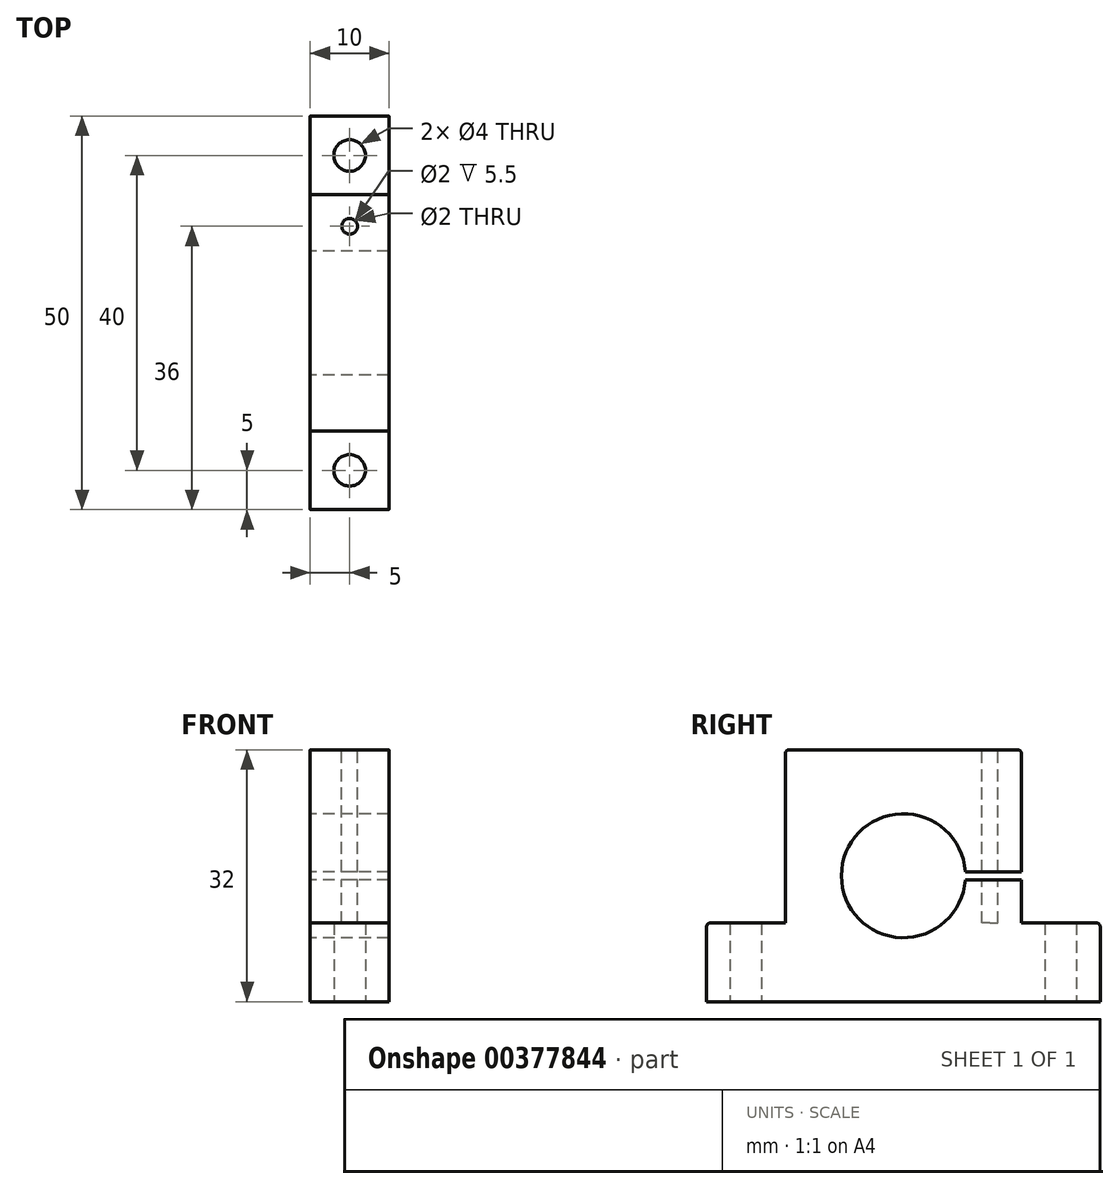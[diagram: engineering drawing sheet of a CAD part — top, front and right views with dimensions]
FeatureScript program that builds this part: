
annotation { "Feature Type Name" : "Feature", "Feature Type Description" : "" }
export const myFeature = defineFeature(function(context is Context, id is Id, definition is map)
    precondition{}
    {
        {
            var Q0;
            Q0=qCreatedBy(makeId("Right.planeOp"),FACE);
            var sketch = newSketch(context, id + "F0", { "sketchPlane" : qUnion([Q0])});
            skLineSegment(sketch, "E0.bottom", {"start": v(15, 16) * mm, "end": v(-15, 16) * mm});
            skLineSegment(sketch, "E0.top", {"start": v(15, -16) * mm, "end": v(-15, -16) * mm});
            skLineSegment(sketch, "E0.left", {"start": v(15, 16) * mm, "end": v(15, 0.5) * mm});
            skLineSegment(sketch, "E0.right", {"start": v(-15, 16) * mm, "end": v(-15, -16) * mm});
            skPoint(sketch, "E0.middle", {"position": v(0, 0) * mm});
            skArc(sketch, "E1", {"start": v(7.86, 0.5) * mm, "mid": v(-7.88, 0) * mm, "end": v(7.86, -0.5) * mm});
            skLineSegment(sketch, "E2", {"start": v(7.86, 0.5) * mm, "end": v(15, 0.5) * mm});
            skLineSegment(sketch, "E3", {"start": v(7.86, -0.5) * mm, "end": v(15, -0.5) * mm});
            skLineSegment(sketch, "E4", {"start": v(0, 0) * mm, "end": v(26.33, 0) * mm, "construction": true});
            skLineSegment(sketch, "E5.trimOffspring", {"start": v(15, -0.5) * mm, "end": v(15, -16) * mm});
            skSolve(sketch);
        }
        {
            var Q0;
            Q0 = qSketchRegion(id + "F0", true);
            extrude(context, id + "F1", {"entities" : qUnion([Q0]), "depth" : 5 * mm, "hasSecondDirection" : true, "secondDirectionOppositeDirection" : true, "secondDirectionDepth" : 5 * mm});
        }
        {
            var Q0;
            Q0=makeQuery(id+"F1.opExtrude","SWEPT_FACE",FACE,{"disambiguationData":[OSD([sQuery(id+"F0.wireOp",EDGE,"E0.bottom")])]});
            var sketch = newSketch(context, id + "F2", { "sketchPlane" : qUnion([Q0])});
            skCircle(sketch, "E6", {"center": v(0, 11) * mm, "radius": 1 * mm});
            skSolve(sketch);
        }
        {
            var Q0;
            Q0 = qSketchRegion(id + "F2", true);
            extrude(context, id + "F3", {"entities" : qUnion([Q0]), "operationType" : NewBodyOperationType.REMOVE, "endBound" : BoundingType.THROUGH_ALL, "oppositeDirection" : true, "depth" : 25 * mm});
        }
        {
            var Q0;
            Q0=makeQuery(id+"F1.opExtrude","SWEPT_FACE",FACE,{"disambiguationData":[OSD([sQuery(id+"F0.wireOp",EDGE,"E0.top")])]});
            var sketch = newSketch(context, id + "F4", { "sketchPlane" : qUnion([Q0])});
            skLineSegment(sketch, "E7.bottom", {"start": v(5, -25) * mm, "end": v(-5, -25) * mm});
            skLineSegment(sketch, "E7.top", {"start": v(5, 25) * mm, "end": v(-5, 25) * mm});
            skLineSegment(sketch, "E7.left", {"start": v(5, -25) * mm, "end": v(5, 25) * mm});
            skLineSegment(sketch, "E7.right", {"start": v(-5, -25) * mm, "end": v(-5, 25) * mm});
            skPoint(sketch, "E7.middle", {"position": v(0, 0) * mm});
            skCircle(sketch, "E8", {"center": v(0, 20) * mm, "radius": 2 * mm});
            skPoint(sketch, "E8.centerSnap0", {"position": v(0, 15) * mm});
            skCircle(sketch, "E9", {"center": v(0, -20) * mm, "radius": 2 * mm});
            skSolve(sketch);
        }
        {
            var Q0;
            Q0 = qSketchRegion(id + "F4", true);
            extrude(context, id + "F5", {"entities" : qUnion([Q0]), "operationType" : NewBodyOperationType.ADD, "oppositeDirection" : true, "depth" : 10 * mm});
        }
        {
            var Q0;
            Q0=makeQuery(id+"F5.boolean.opBoolean","MERGE",FACE,{"derivedFrom":[makeQuery(id+"F1.opExtrude","CAP_FACE",FACE,{"disambiguationData":[OSD([sQuery(id+"F0.wireOp",EDGE,"E0.bottom"),sQuery(id+"F0.wireOp",EDGE,"E0.top"),sQuery(id+"F0.wireOp",EDGE,"E0.left"),sQuery(id+"F0.wireOp",EDGE,"E0.right"),sQuery(id+"F0.wireOp",EDGE,"E1"),sQuery(id+"F0.wireOp",EDGE,"E2"),sQuery(id+"F0.wireOp",EDGE,"E3"),sQuery(id+"F0.wireOp",EDGE,"E5.trimOffspring")])],"isStart":false}),makeQuery(id+"F5.opExtrude","SWEPT_FACE",FACE,{"disambiguationData":[OSD([sQuery(id+"F4.wireOp",EDGE,"E7.left")])]})]});
            var sketch = newSketch(context, id + "F6", { "sketchPlane" : qUnion([Q0])});
            skCircle(sketch, "E10", {"center": v(0, 0) * mm, "radius": 7.88 * mm});
            skSolve(sketch);
        }
        {
            var Q0;
            Q0 = qSketchRegion(id + "F6", true);
            extrude(context, id + "F7", {"entities" : qUnion([Q0]), "operationType" : NewBodyOperationType.REMOVE, "endBound" : BoundingType.THROUGH_ALL, "oppositeDirection" : true, "depth" : 25 * mm});
        }
        {
            var Q0;
            Q0=makeQuery(id+"F1.opExtrude","SWEPT_EDGE",EDGE,{"disambiguationData":[OSD([sQuery(id+"F0.wireOp",EDGE,"E0.bottom"),sQuery(id+"F0.wireOp",EDGE,"E0.right")])]});
            var Q1;
            Q1=makeQuery(id+"F1.opExtrude","SWEPT_EDGE",EDGE,{"disambiguationData":[OSD([sQuery(id+"F0.wireOp",EDGE,"E0.bottom"),sQuery(id+"F0.wireOp",EDGE,"E0.left")])]});
            var Q2;
            Q2=makeQuery(id+"F5.opExtrude","CAP_EDGE",EDGE,{"disambiguationData":[OSD([sQuery(id+"F4.wireOp",EDGE,"E7.top")])],"isStart":false});
            var Q3;
            Q3=makeQuery(id+"F5.opExtrude","CAP_EDGE",EDGE,{"disambiguationData":[OSD([sQuery(id+"F4.wireOp",EDGE,"E7.bottom")])],"isStart":false});
            fillet(context, id + "F8", {"entities" : qUnion([Q0, Q1, Q2, Q3]), "radius" : .5 * mm, "tangentPropagation" : true, "allowEdgeOverflow" : false});
        }
    });
